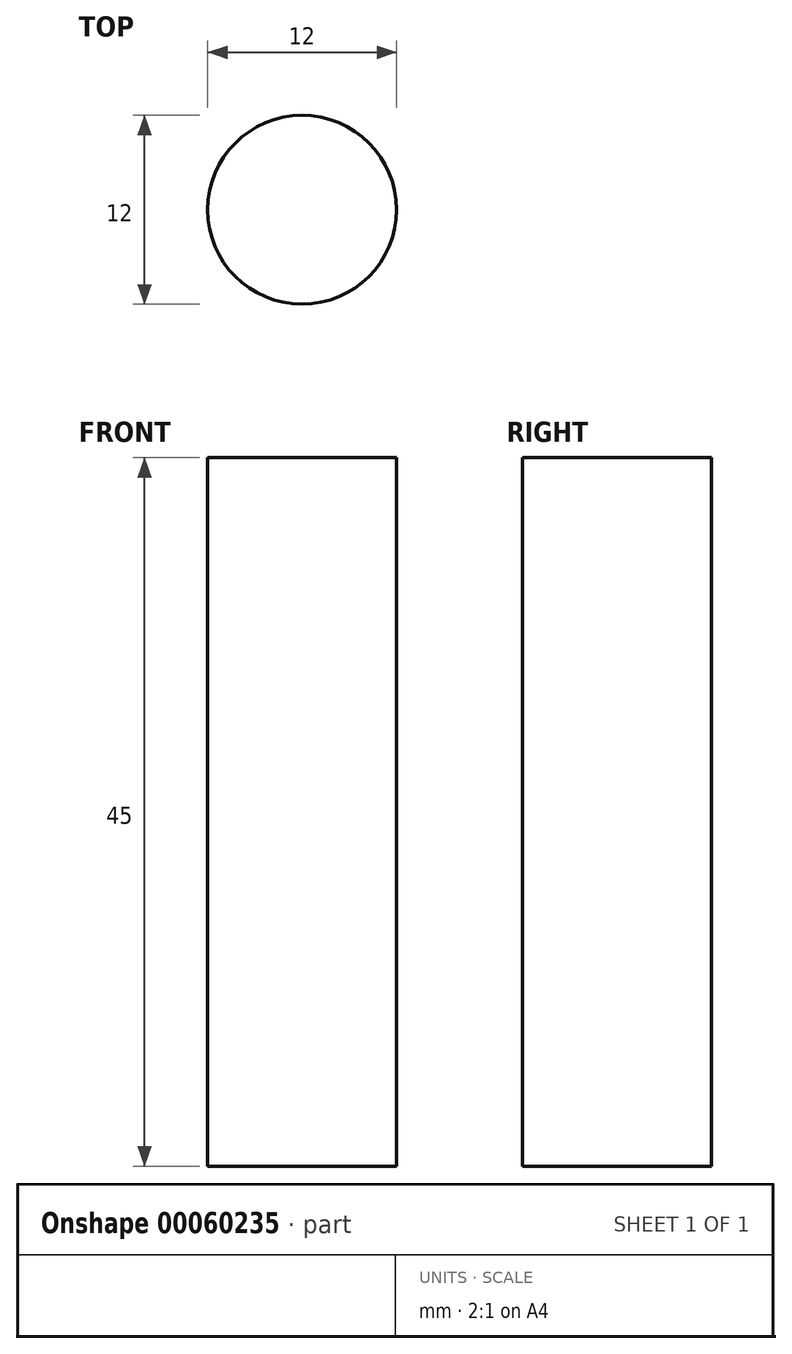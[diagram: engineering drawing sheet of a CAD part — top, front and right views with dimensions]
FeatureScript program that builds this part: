
annotation { "Feature Type Name" : "Feature", "Feature Type Description" : "" }
export const myFeature = defineFeature(function(context is Context, id is Id, definition is map)
    precondition{}
    {
        {
            var Q0;
            Q0=qCreatedBy(makeId("Top.planeOp"),FACE);
            var sketch = newSketch(context, id + "F0", { "sketchPlane" : qUnion([Q0])});
            skCircle(sketch, "E0", {"center": v(0, 0) * mm, "radius": 6 * mm});
            skSolve(sketch);
        }
        {
            var Q0;
            Q0 = qSketchRegion(id + "F0", true);
            extrude(context, id + "F1", {"entities" : qUnion([Q0]), "depth" : 45 * mm});
        }
    });
